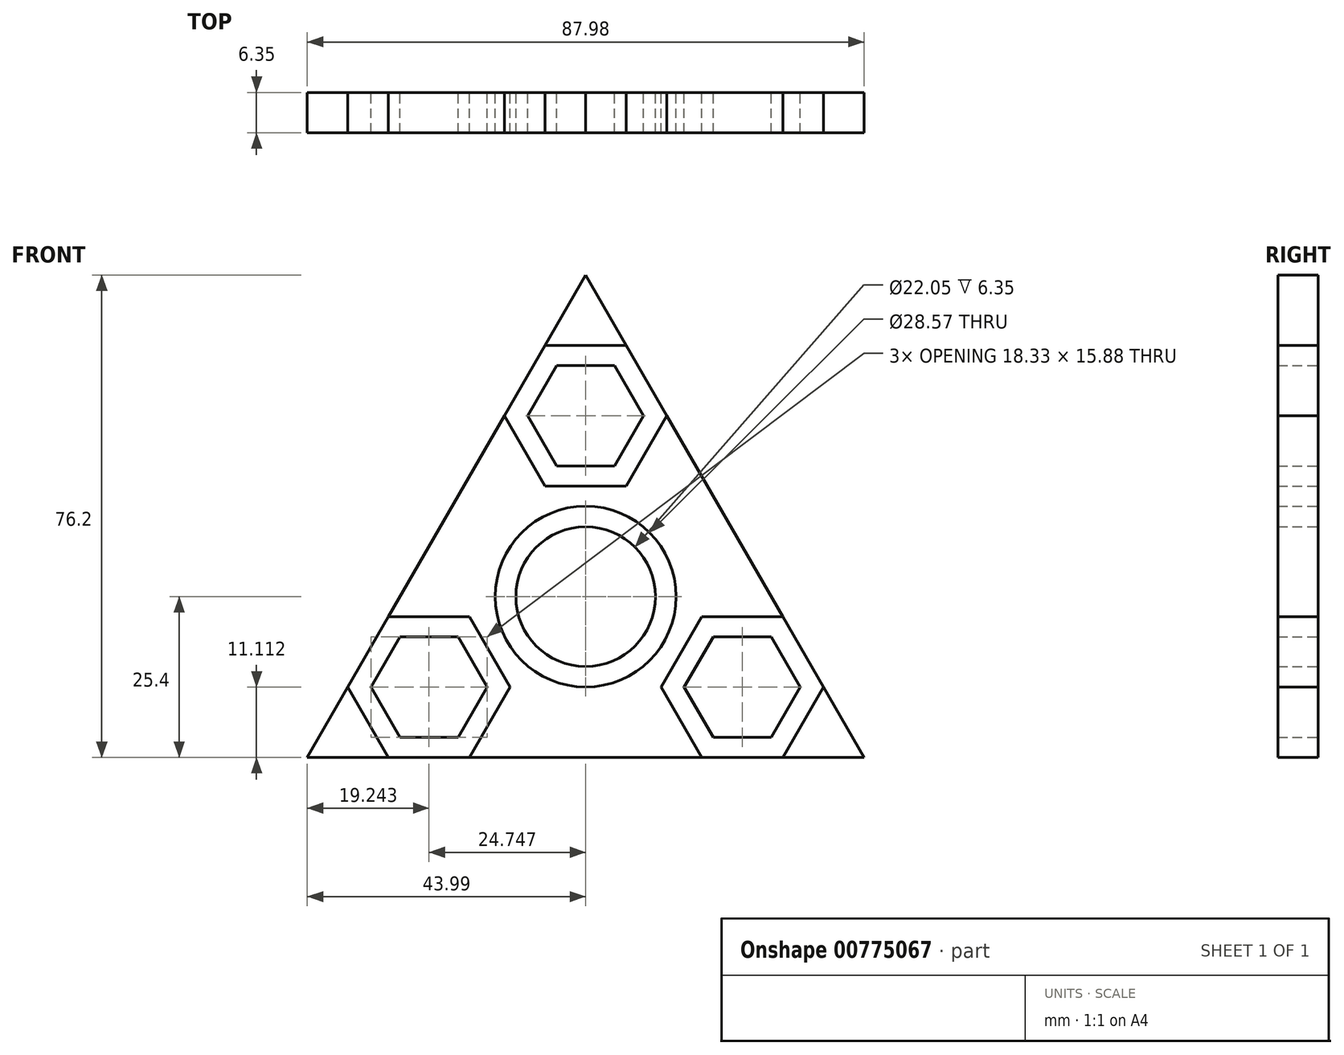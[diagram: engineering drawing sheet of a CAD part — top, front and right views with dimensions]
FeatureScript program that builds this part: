
annotation { "Feature Type Name" : "Feature", "Feature Type Description" : "" }
export const myFeature = defineFeature(function(context is Context, id is Id, definition is map)
    precondition{}
    {
        {
            var Q0;
            Q0=qCreatedBy(makeId("Front.planeOp"),FACE);
            var sketch = newSketch(context, id + "F0", { "sketchPlane" : qUnion([Q0])});
            skCircle(sketch, "E0", {"center": v(0, 0) * mm, "radius": 11.02 * mm});
            skCircle(sketch, "E1", {"center": v(0, 0) * mm, "radius": 14.29 * mm});
            skCircle(sketch, "E2.cCircle", {"center": v(0, 28.58) * mm, "radius": 7.94 * mm, "construction": true});
            skLineSegment(sketch, "E2.0", {"start": v(4.58, 20.64) * mm, "end": v(-4.58, 20.64) * mm});
            skLineSegment(sketch, "E2.1", {"start": v(-4.58, 20.64) * mm, "end": v(-9.17, 28.58) * mm});
            skLineSegment(sketch, "E2.2", {"start": v(-9.17, 28.58) * mm, "end": v(-4.58, 36.51) * mm});
            skLineSegment(sketch, "E2.3", {"start": v(-4.58, 36.51) * mm, "end": v(4.58, 36.51) * mm});
            skLineSegment(sketch, "E2.4", {"start": v(4.58, 36.51) * mm, "end": v(9.17, 28.57) * mm});
            skLineSegment(sketch, "E2.5", {"start": v(9.17, 28.57) * mm, "end": v(4.58, 20.64) * mm});
            skPoint(sketch, "E2.0.midPoint", {"position": v(0, 20.64) * mm});
            skCircle(sketch, "E3.cCircle", {"center": v(0, 28.58) * mm, "radius": 11.11 * mm, "construction": true});
            skLineSegment(sketch, "E3.0", {"start": v(6.42, 17.46) * mm, "end": v(-6.42, 17.46) * mm});
            skLineSegment(sketch, "E3.1", {"start": v(-6.42, 17.46) * mm, "end": v(-12.83, 28.57) * mm});
            skLineSegment(sketch, "E3.2", {"start": v(-12.83, 28.57) * mm, "end": v(-6.42, 39.69) * mm});
            skLineSegment(sketch, "E3.3", {"start": v(-6.42, 39.69) * mm, "end": v(6.42, 39.69) * mm});
            skLineSegment(sketch, "E3.4", {"start": v(6.42, 39.69) * mm, "end": v(12.83, 28.58) * mm});
            skLineSegment(sketch, "E3.5", {"start": v(12.83, 28.58) * mm, "end": v(6.42, 17.46) * mm});
            skPoint(sketch, "E3.0.midPoint", {"position": v(0, 17.46) * mm});
            skCircle(sketch, "E4.1.0", {"center": v(-24.75, -14.29) * mm, "radius": 7.94 * mm, "construction": true});
            skLineSegment(sketch, "E4.1.1", {"start": v(-20.16, -6.35) * mm, "end": v(-15.58, -14.29) * mm});
            skPoint(sketch, "E4.1.2", {"position": v(-15.12, -8.73) * mm});
            skLineSegment(sketch, "E4.1.3", {"start": v(-20.16, -22.22) * mm, "end": v(-29.33, -22.22) * mm});
            skLineSegment(sketch, "E4.1.4", {"start": v(-31.16, -3.17) * mm, "end": v(-18.33, -3.17) * mm});
            skLineSegment(sketch, "E4.1.5", {"start": v(-37.58, -14.29) * mm, "end": v(-31.16, -3.17) * mm});
            skLineSegment(sketch, "E4.1.6", {"start": v(-31.16, -25.4) * mm, "end": v(-37.58, -14.29) * mm});
            skLineSegment(sketch, "E4.1.7", {"start": v(-15.58, -14.29) * mm, "end": v(-20.16, -22.23) * mm});
            skLineSegment(sketch, "E4.1.8", {"start": v(-29.33, -22.22) * mm, "end": v(-33.91, -14.29) * mm});
            skLineSegment(sketch, "E4.1.9", {"start": v(-33.91, -14.29) * mm, "end": v(-29.33, -6.35) * mm});
            skLineSegment(sketch, "E4.1.10", {"start": v(-29.33, -6.35) * mm, "end": v(-20.16, -6.35) * mm});
            skCircle(sketch, "E4.1.11", {"center": v(-24.75, -14.29) * mm, "radius": 11.11 * mm, "construction": true});
            skLineSegment(sketch, "E4.1.12", {"start": v(-18.33, -3.17) * mm, "end": v(-11.92, -14.29) * mm});
            skLineSegment(sketch, "E4.1.13", {"start": v(-11.92, -14.29) * mm, "end": v(-18.33, -25.4) * mm});
            skLineSegment(sketch, "E4.1.14", {"start": v(-18.33, -25.4) * mm, "end": v(-31.16, -25.4) * mm});
            skPoint(sketch, "E4.1.15", {"position": v(-17.87, -10.32) * mm});
            skCircle(sketch, "E4.2.0", {"center": v(24.75, -14.29) * mm, "radius": 7.94 * mm, "construction": true});
            skLineSegment(sketch, "E4.2.1", {"start": v(15.58, -14.29) * mm, "end": v(20.16, -6.35) * mm});
            skPoint(sketch, "E4.2.2", {"position": v(15.12, -8.73) * mm});
            skLineSegment(sketch, "E4.2.3", {"start": v(29.33, -6.35) * mm, "end": v(33.91, -14.29) * mm});
            skLineSegment(sketch, "E4.2.4", {"start": v(18.33, -25.4) * mm, "end": v(11.92, -14.29) * mm});
            skLineSegment(sketch, "E4.2.5", {"start": v(31.16, -25.4) * mm, "end": v(18.33, -25.4) * mm});
            skLineSegment(sketch, "E4.2.6", {"start": v(37.58, -14.29) * mm, "end": v(31.16, -25.4) * mm});
            skLineSegment(sketch, "E4.2.7", {"start": v(20.16, -6.35) * mm, "end": v(29.33, -6.35) * mm});
            skLineSegment(sketch, "E4.2.8", {"start": v(33.91, -14.29) * mm, "end": v(29.33, -22.23) * mm});
            skLineSegment(sketch, "E4.2.9", {"start": v(29.33, -22.23) * mm, "end": v(20.16, -22.23) * mm});
            skLineSegment(sketch, "E4.2.10", {"start": v(20.16, -22.23) * mm, "end": v(15.58, -14.29) * mm});
            skCircle(sketch, "E4.2.11", {"center": v(24.75, -14.29) * mm, "radius": 11.11 * mm, "construction": true});
            skLineSegment(sketch, "E4.2.12", {"start": v(11.92, -14.29) * mm, "end": v(18.33, -3.18) * mm});
            skLineSegment(sketch, "E4.2.13", {"start": v(18.33, -3.18) * mm, "end": v(31.16, -3.18) * mm});
            skLineSegment(sketch, "E4.2.14", {"start": v(31.16, -3.18) * mm, "end": v(37.58, -14.29) * mm});
            skPoint(sketch, "E4.2.15", {"position": v(17.87, -10.32) * mm});
            skSolve(sketch);
        }
        {
            var Q0;
            Q0=qCreatedBy(makeId("Front.planeOp"),FACE);
            var sketch = newSketch(context, id + "F1", { "sketchPlane" : qUnion([Q0])});
            skLineSegment(sketch, "E5.0", {"start": v(-4.58, 20.64) * mm, "end": v(-9.17, 28.58) * mm});
            skLineSegment(sketch, "E5.1", {"start": v(4.58, 20.64) * mm, "end": v(-4.58, 20.64) * mm});
            skLineSegment(sketch, "E5.2", {"start": v(-9.17, 28.58) * mm, "end": v(-4.58, 36.51) * mm});
            skCircle(sketch, "E5.3", {"center": v(0, 28.58) * mm, "radius": 7.94 * mm});
            skLineSegment(sketch, "E5.4", {"start": v(-4.58, 36.51) * mm, "end": v(4.58, 36.51) * mm});
            skLineSegment(sketch, "E5.5", {"start": v(4.58, 36.51) * mm, "end": v(9.17, 28.57) * mm});
            skLineSegment(sketch, "E5.6", {"start": v(18.33, -3.18) * mm, "end": v(31.16, -3.18) * mm});
            skCircle(sketch, "E5.7", {"center": v(-24.75, -14.29) * mm, "radius": 11.11 * mm});
            skCircle(sketch, "E5.8", {"center": v(0, 0) * mm, "radius": 14.29 * mm});
            skCircle(sketch, "E5.9", {"center": v(0, 0) * mm, "radius": 11.02 * mm});
            skLineSegment(sketch, "E5.10", {"start": v(12.83, 28.58) * mm, "end": v(6.42, 17.46) * mm});
            skLineSegment(sketch, "E5.11", {"start": v(6.42, 39.69) * mm, "end": v(12.83, 28.58) * mm});
            skLineSegment(sketch, "E5.12", {"start": v(-6.42, 39.69) * mm, "end": v(6.42, 39.69) * mm});
            skLineSegment(sketch, "E5.13", {"start": v(37.58, -14.29) * mm, "end": v(31.16, -25.4) * mm});
            skLineSegment(sketch, "E5.14", {"start": v(-31.16, -3.17) * mm, "end": v(-18.33, -3.17) * mm});
            skLineSegment(sketch, "E5.15", {"start": v(9.17, 28.57) * mm, "end": v(4.58, 20.64) * mm});
            skCircle(sketch, "E5.16", {"center": v(0, 28.58) * mm, "radius": 11.11 * mm});
            skLineSegment(sketch, "E5.17", {"start": v(6.42, 17.46) * mm, "end": v(-6.42, 17.46) * mm});
            skLineSegment(sketch, "E5.18", {"start": v(-6.42, 17.46) * mm, "end": v(-12.83, 28.57) * mm});
            skLineSegment(sketch, "E5.19", {"start": v(-12.83, 28.57) * mm, "end": v(-6.42, 39.69) * mm});
            skLineSegment(sketch, "E5.20", {"start": v(31.16, -3.18) * mm, "end": v(37.58, -14.29) * mm});
            skLineSegment(sketch, "E5.21", {"start": v(-18.33, -3.17) * mm, "end": v(-11.92, -14.29) * mm});
            skLineSegment(sketch, "E5.22", {"start": v(20.16, -22.23) * mm, "end": v(15.58, -14.29) * mm});
            skLineSegment(sketch, "E5.23", {"start": v(-29.33, -22.22) * mm, "end": v(-33.91, -14.29) * mm});
            skLineSegment(sketch, "E5.24", {"start": v(-37.58, -14.29) * mm, "end": v(-31.16, -3.17) * mm});
            skLineSegment(sketch, "E5.25", {"start": v(20.16, -6.35) * mm, "end": v(29.33, -6.35) * mm});
            skLineSegment(sketch, "E5.26", {"start": v(-18.33, -25.4) * mm, "end": v(-31.16, -25.4) * mm});
            skCircle(sketch, "E5.27", {"center": v(-24.75, -14.29) * mm, "radius": 7.94 * mm});
            skLineSegment(sketch, "E5.28", {"start": v(29.33, -6.35) * mm, "end": v(33.91, -14.29) * mm});
            skLineSegment(sketch, "E5.29", {"start": v(-11.92, -14.29) * mm, "end": v(-18.33, -25.4) * mm});
            skCircle(sketch, "E5.30", {"center": v(24.75, -14.29) * mm, "radius": 11.11 * mm});
            skLineSegment(sketch, "E5.31", {"start": v(-33.91, -14.29) * mm, "end": v(-29.33, -6.35) * mm});
            skLineSegment(sketch, "E5.32", {"start": v(-31.16, -25.4) * mm, "end": v(-37.58, -14.29) * mm});
            skCircle(sketch, "E5.33", {"center": v(24.75, -14.29) * mm, "radius": 7.94 * mm});
            skLineSegment(sketch, "E5.34", {"start": v(33.91, -14.29) * mm, "end": v(29.33, -22.23) * mm});
            skLineSegment(sketch, "E5.35", {"start": v(-20.16, -6.35) * mm, "end": v(-15.58, -14.29) * mm});
            skLineSegment(sketch, "E5.36", {"start": v(18.33, -25.4) * mm, "end": v(11.92, -14.29) * mm});
            skLineSegment(sketch, "E5.37", {"start": v(11.92, -14.29) * mm, "end": v(18.33, -3.18) * mm});
            skLineSegment(sketch, "E5.38", {"start": v(-29.33, -6.35) * mm, "end": v(-20.16, -6.35) * mm});
            skLineSegment(sketch, "E5.39", {"start": v(-15.58, -14.29) * mm, "end": v(-20.16, -22.23) * mm});
            skLineSegment(sketch, "E5.40", {"start": v(15.58, -14.29) * mm, "end": v(20.16, -6.35) * mm});
            skLineSegment(sketch, "E5.41", {"start": v(29.33, -22.23) * mm, "end": v(20.16, -22.23) * mm});
            skLineSegment(sketch, "E5.42", {"start": v(-20.16, -22.22) * mm, "end": v(-29.33, -22.22) * mm});
            skLineSegment(sketch, "E5.43", {"start": v(31.16, -25.4) * mm, "end": v(18.33, -25.4) * mm});
            skLineSegment(sketch, "E6", {"start": v(-31.16, -3.17) * mm, "end": v(-12.83, 28.57) * mm});
            skLineSegment(sketch, "E7", {"start": v(12.83, 28.58) * mm, "end": v(31.16, -3.18) * mm});
            skLineSegment(sketch, "E8", {"start": v(-18.33, -25.4) * mm, "end": v(18.33, -25.4) * mm});
            skLineSegment(sketch, "E9", {"start": v(-6.42, 39.69) * mm, "end": v(0, 50.8) * mm});
            skPoint(sketch, "E9.endSnap0", {"position": v(0, 36.51) * mm});
            skLineSegment(sketch, "E10", {"start": v(0, 50.8) * mm, "end": v(6.42, 39.69) * mm});
            skLineSegment(sketch, "E11", {"start": v(-37.58, -14.29) * mm, "end": v(-44, -25.4) * mm});
            skLineSegment(sketch, "E12", {"start": v(-44, -25.4) * mm, "end": v(-31.16, -25.4) * mm});
            skLineSegment(sketch, "E13", {"start": v(31.16, -25.4) * mm, "end": v(43.99, -25.4) * mm});
            skLineSegment(sketch, "E14", {"start": v(43.99, -25.4) * mm, "end": v(37.58, -14.29) * mm});
            skSolve(sketch);
        }
        {
            var Q0;
            Q0 = qSketchRegion(id + "F0", true);
            var Q1;
            Q1=makeQuery(id+"F1.imprint","IMPRINT",FACE,{"disambiguationData":[TD([[makeQuery(id+"F1.imprint","IMPRINT",EDGE,{"derivedFrom":sQuery(id+"F1.wireOp",EDGE,"E5.8")}),-1.0]])]});
            var Q2;
            {var subQ0=sQuery(id+"F1.wireOp",EDGE,"E9");Q2=makeQuery(id+"F1.imprint","IMPRINT",FACE,{"disambiguationData":[TD([[makeQuery(id+"F1.imprint","IMPRINT",EDGE,{"derivedFrom":subQ0}),-1.0]])]});}
            var Q3;
            {var subQ3=sQuery(id+"F1.wireOp",EDGE,"E13");Q3=makeQuery(id+"F1.imprint","IMPRINT",FACE,{"disambiguationData":[TD([[makeQuery(id+"F1.imprint","IMPRINT",EDGE,{"derivedFrom":subQ3}),1.0]])]});}
            var Q4;
            {var subQ3=sQuery(id+"F1.wireOp",EDGE,"E11");Q4=makeQuery(id+"F1.imprint","IMPRINT",FACE,{"disambiguationData":[TD([[makeQuery(id+"F1.imprint","IMPRINT",EDGE,{"derivedFrom":subQ3}),1.0]])]});}
            extrude(context, id + "F2", {"entities" : qUnion([Q0, Q1, Q2, Q3, Q4]), "depth" : 6.35 * mm, "offsetDistance" : 25.4 * mm});
        }
    });
